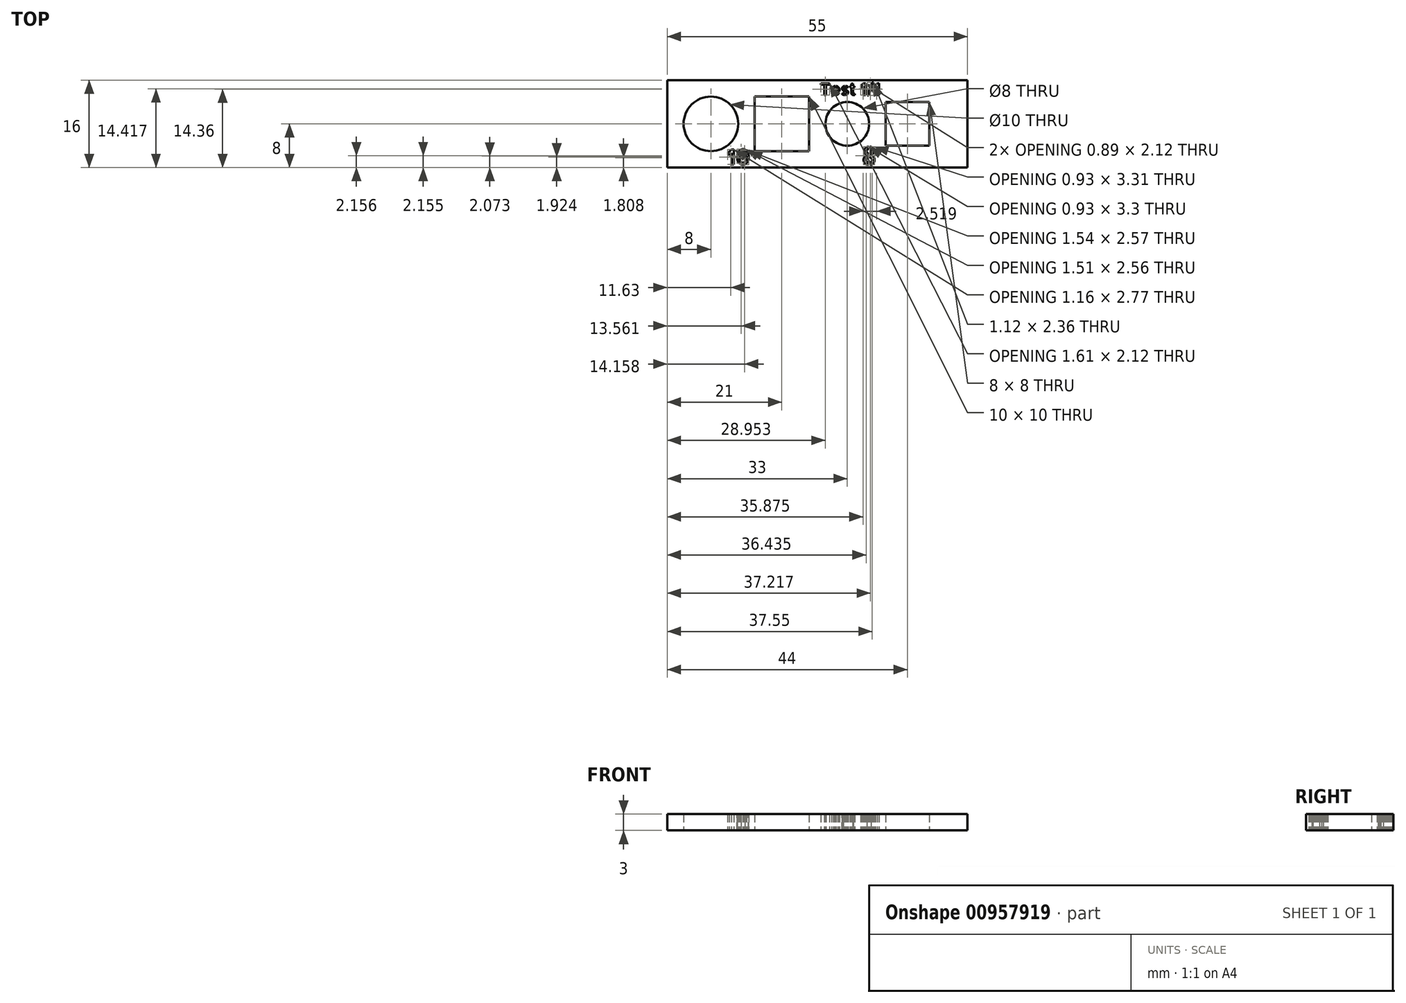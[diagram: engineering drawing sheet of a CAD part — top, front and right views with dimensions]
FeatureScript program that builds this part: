
annotation { "Feature Type Name" : "Feature", "Feature Type Description" : "" }
export const myFeature = defineFeature(function(context is Context, id is Id, definition is map)
    precondition{}
    {
        {
            var Q0;
            Q0=qCreatedBy(makeId("Top.planeOp"),FACE);
            var sketch = newSketch(context, id + "F0", { "sketchPlane" : qUnion([Q0])});
            skCircle(sketch, "E0", {"center": v(-19.5, 0) * mm, "radius": 5 * mm});
            skPoint(sketch, "E1.middle", {"position": v(5.5, 0) * mm});
            skPoint(sketch, "E2.middle", {"position": v(16.5, 0) * mm});
            skLineSegment(sketch, "E3.bottom", {"start": v(-1.5, 5) * mm, "end": v(-11.5, 5) * mm});
            skLineSegment(sketch, "E3.top", {"start": v(-1.5, -5) * mm, "end": v(-11.5, -5) * mm});
            skLineSegment(sketch, "E3.left", {"start": v(-1.5, 5) * mm, "end": v(-1.5, -5) * mm});
            skLineSegment(sketch, "E3.right", {"start": v(-11.5, 5) * mm, "end": v(-11.5, -5) * mm});
            skPoint(sketch, "E3.middle", {"position": v(-6.5, 0) * mm});
            skCircle(sketch, "E4", {"center": v(5.5, 0) * mm, "radius": 4 * mm});
            skLineSegment(sketch, "E5.bottom", {"start": v(12.5, 4) * mm, "end": v(20.5, 4) * mm});
            skLineSegment(sketch, "E5.top", {"start": v(12.5, -4) * mm, "end": v(20.5, -4) * mm});
            skLineSegment(sketch, "E5.left", {"start": v(12.5, 4) * mm, "end": v(12.5, -4) * mm});
            skLineSegment(sketch, "E5.right", {"start": v(20.5, 4) * mm, "end": v(20.5, -4) * mm});
            skLineSegment(sketch, "E6", {"start": v(-14.5, 0) * mm, "end": v(-11.5, 0) * mm, "construction": true});
            skLineSegment(sketch, "E7", {"start": v(-1.5, 0) * mm, "end": v(1.5, 0) * mm, "construction": true});
            skLineSegment(sketch, "E8", {"start": v(9.5, 0) * mm, "end": v(12.5, 0) * mm, "construction": true});
            skLineSegment(sketch, "E9.bottom", {"start": v(27.5, 8) * mm, "end": v(-27.5, 8) * mm});
            skLineSegment(sketch, "E9.top", {"start": v(27.5, -8) * mm, "end": v(-27.5, -8) * mm});
            skLineSegment(sketch, "E9.left", {"start": v(27.5, 8) * mm, "end": v(27.5, -8) * mm});
            skLineSegment(sketch, "E9.right", {"start": v(-27.5, 8) * mm, "end": v(-27.5, -8) * mm});
            skPoint(sketch, "E9.middle", {"position": v(0, 0) * mm});
            skSolve(sketch);
        }
        {
            var Q0;
            Q0=qCreatedBy(makeId("Top.planeOp"),FACE);
            var sketch = newSketch(context, id + "F1", { "sketchPlane" : qUnion([Q0])});
            skText(sketch, "E10", { "text": "Test 1/1", "fontName": "AllertaStencil-Regular.ttf"});
            skText(sketch, "E11", { "text": "10", "fontName": "AllertaStencil-Regular.ttf"});
            skText(sketch, "E12", { "text": "8", "fontName": "AllertaStencil-Regular.ttf"});
            const initialGuessF1  = {"E10": [0.0005, 0.0053, 1, 0, 0.00212], "E11": [-0.01656, -0.00746, 1, 0, 0.00277], "E12": [0.00815, -0.00746, 1, 0, 0.00325]};
            skSetInitialGuess(sketch, initialGuessF1);
            skSolve(sketch);
        }
        {
            var Q0;
            Q0=makeQuery(id+"F0.imprint","IMPRINT",FACE,{"disambiguationData":[TD([[makeQuery(id+"F0.imprint","IMPRINT",EDGE,{"derivedFrom":sQuery(id+"F0.wireOp",EDGE,"E0")}),-1.0]])]});
            extrude(context, id + "F2", {"entities" : qUnion([Q0]), "depth" : 3 * mm, "offsetDistance" : 25 * mm});
        }
        {
            var Q0;
            Q0 = qSketchRegion(id + "F1", true);
            extrude(context, id + "F3", {"entities" : qUnion([Q0]), "operationType" : NewBodyOperationType.REMOVE, "endBound" : BoundingType.THROUGH_ALL, "depth" : 3 * mm, "offsetDistance" : 25 * mm});
        }
    });
